# Revit family: equip-sink-elkay-lav-wall-elvacm
name_source: partatom
category: Plumbing Fixtures
units: mm (PartAtom-declared; Revit-internal decimal feet)

## family parameters
Cut with Voids When Loaded = No
Host = Face
Part Type = Normal
Room Calculation Point = No
Round Connector Dimension = Use Radius
Shared = No

## types (8) — shared parameters
Assembly Code = D2010410
Backsplash Height = 0' - 2 1/2"
Bowl Depth = 0' - 5 1/2"
Bowl Drain Location FB = 0' - 3 1/2"
Bowl Length = 1' - 4"
Bowl Width = 0' - 11 1/2"
Bubbler CW Flow Rate = 2 GPM
Bubbler Material = Metal - Steel - Stainless - Chrome
Bubbler Nominal Dia = 0' - 0 1/2"
Bubbler Nominal Radius = 0' - 0 1/4"
CW Flow Rate = 2 GPM
Cost = 1 $
Default Elevation = 2' - 7 1/2"
Description = Wash-Up Lavatory Sinks
Drain CL LR to Left Bowl Edge = 0' - 8"
Drain Material = Metal - Steel - Stainless - Chrome
Faucet Hole Dia = 0' - 1 1/4"
Faucet Hole One = No
Faucet Hole One Top = 0' - 0 1/8"
Faucet Hole One to CL = 0' - 4"
Faucet Hole Three = No
Faucet Hole Three Top = 0' - 0 1/8"
Faucet Hole Two = Yes
Faucet Hole Two Top = 0' - 0 1/4"
Faucet Material = Metal - Steel - Stainless - Chrome
Faucet Part = LKB721C
Faucet Water Supply Radius = 0' - 0 3/16"
HW Flow Rate = 2 GPM
Hole One to Three = 0' - 8"
Hole One to Two = 0' - 4"
Hole Radius = 0' - 0 5/8"
Keynote = D2010410
Manufacturer = Elkay Manufacturing
MasterFormat Number = 22.42.16.16
MasterFormat Title = Commercial Sinks
Nominal Dia = 0' - 0 1/2"
Nominal Radius = 0' - 0 1/4"
OmniClass Code = 23.45.05.14.14.27
OmniClass Title = Service Sinks
Reference Level to Back Plane = 0' - 0"
Sanitary Flow Rate = 10 GPM
Sanitary Nominal Dia = 0' - 1 1/2"
Sanitary Nominal Radius = 0' - 0 3/4"
Sink Ledge Back Width = 0' - 4 1/2"
Sink Ledge Back Width Hidden = 0' - 4 1/2"
Sink Ledge Front Width = 0' - 3"
Sink Ledge Front Width Hidden = 0' - 3"
Sink Ledge Left Width = 0' - 3"
Sink Ledge Left Width Hidden = 0' - 3"
Sink Ledge Right Width = 0' - 3"
Sink Ledge Right Width Hidden = 0' - 3"
Sink Length = 1' - 10"
Sink Material = Metal - Steel - Stainless - Chrome
Sink San Conn Extr Visibility = No
Sink Width = 1' - 7"
Specification Sheet URL = http://www.elkayusa.com
Stem Material = Metal - Steel
Thermostatic Mix Valve = No
URL = www.elkayusa.com
Valve Material = Metal - Steel - Stainless - Chrome
Vent Connection = Yes
zero-valued in all types: CWFU, HWFU, WFU

## per-type parameters (varying)
| type | AC Power | Mechanical Mix Valve | Mix Valve Part | No Mix Valve | OverFlow | Overflow Void | Supply Line Mix Length |
| ELV2219SACMC | Yes | Yes | LK724 | No | No | 0' - 0 1/16" | 0' - 0 1/2" |
| ELV2219SBMC | No | Yes | LK724 | No | No | 0' - 0 1/16" | 0' - 0 1/2" |
| ELV2219SACC | Yes | No |  | Yes | No | 0' - 0 1/16" | 0' - 2" |
| ELV2219SBC | No | No |  | Yes | No | 0' - 0 1/16" | 0' - 2" |
| ELVWO2219SACC | Yes | No |  | Yes | Yes | 0' - 0 3/16" | 0' - 2" |
| ELVWO2219SACMC | Yes | Yes | LK724 | No | Yes | 0' - 0 3/16" | 0' - 0 1/2" |
| ELVWO2219SBC | No | No |  | Yes | Yes | 0' - 0 3/16" | 0' - 2" |
| ELVWO2219SBMC | No | Yes | LK724 | No | Yes | 0' - 0 3/16" | 0' - 0 1/2" |

note: column(s) folded — value = type name in every type: Model, Sink Part

## geometry (parser evidence)
native form markers: Sweep x18
no freeform markers — native parametric forms only
